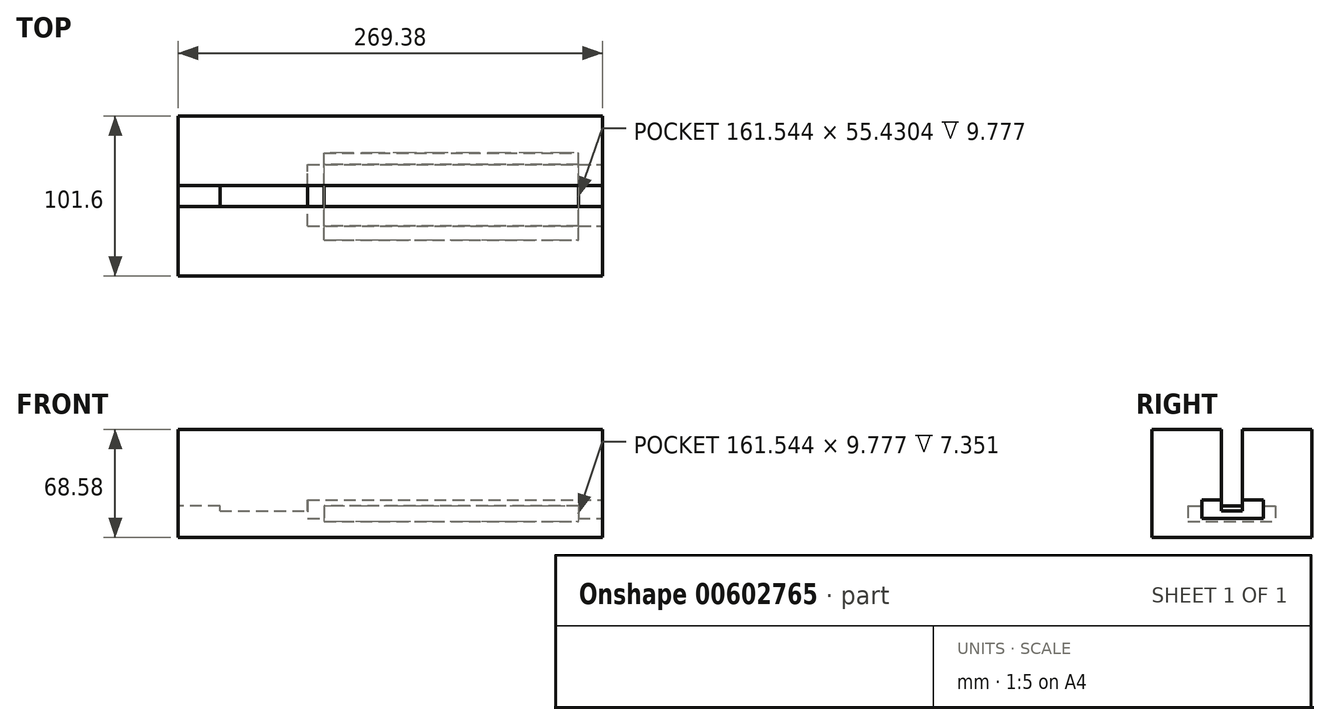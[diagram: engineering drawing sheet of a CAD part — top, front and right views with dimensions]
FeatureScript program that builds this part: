
annotation { "Feature Type Name" : "Feature", "Feature Type Description" : "" }
export const myFeature = defineFeature(function(context is Context, id is Id, definition is map)
    precondition{}
    {
        {
            var Q0;
            Q0=qCreatedBy(makeId("Top.planeOp"),FACE);
            var sketch = newSketch(context, id + "F0", { "sketchPlane" : qUnion([Q0])});
            skLineSegment(sketch, "E0.bottom", {"start": v(-134.7, 50.8) * mm, "end": v(134.7, 50.8) * mm});
            skLineSegment(sketch, "E0.top", {"start": v(-134.7, -50.8) * mm, "end": v(134.7, -50.8) * mm});
            skLineSegment(sketch, "E0.left", {"start": v(-134.7, 50.8) * mm, "end": v(-134.7, -50.8) * mm});
            skLineSegment(sketch, "E0.right", {"start": v(134.7, 50.8) * mm, "end": v(134.7, -50.8) * mm});
            skPoint(sketch, "E0.middle", {"position": v(0, 0) * mm});
            skLineSegment(sketch, "E1.bottom", {"start": v(-134.7, 34.7) * mm, "end": v(134.7, 34.7) * mm});
            skLineSegment(sketch, "E1.top", {"start": v(-134.7, -34.7) * mm, "end": v(134.7, -34.7) * mm});
            skLineSegment(sketch, "E1.left", {"start": v(-134.7, 34.7) * mm, "end": v(-134.7, -34.7) * mm});
            skLineSegment(sketch, "E1.right", {"start": v(134.7, 34.7) * mm, "end": v(134.7, -34.7) * mm});
            skSolve(sketch);
        }
        {
            var Q0;
            Q0 = qSketchRegion(id + "F0", true);
            extrude(context, id + "F1", {"entities" : qUnion([Q0]), "depth" : 68.58 * mm, "offsetDistance" : 25.4 * mm});
        }
        {
            var Q0;
            Q0=makeQuery(id+"F1.opExtrude","CAP_FACE",FACE,{"disambiguationData":[OSD([sQuery(id+"F0.wireOp",EDGE,"E0.bottom"),sQuery(id+"F0.wireOp",EDGE,"E0.top"),sQuery(id+"F0.wireOp",EDGE,"E0.left"),sQuery(id+"F0.wireOp",EDGE,"E0.right"),sQuery(id+"F0.wireOp",EDGE,"E1.left"),sQuery(id+"F0.wireOp",EDGE,"E1.right")])],"isStart":false});
            var sketch = newSketch(context, id + "F2", { "sketchPlane" : qUnion([Q0])});
            skLineSegment(sketch, "E2.bottom", {"start": v(-134.7, 6.75) * mm, "end": v(134.7, 6.75) * mm});
            skLineSegment(sketch, "E2.top", {"start": v(-134.7, -6.75) * mm, "end": v(134.7, -6.75) * mm});
            skLineSegment(sketch, "E2.left", {"start": v(-134.7, 6.75) * mm, "end": v(-134.7, -6.75) * mm});
            skLineSegment(sketch, "E2.right", {"start": v(134.7, 6.75) * mm, "end": v(134.7, -6.75) * mm});
            skPoint(sketch, "E2.middle", {"position": v(0, 0) * mm});
            skSolve(sketch);
        }
        {
            var Q0;
            Q0 = qSketchRegion(id + "F2", true);
            extrude(context, id + "F3", {"entities" : qUnion([Q0]), "operationType" : NewBodyOperationType.REMOVE, "oppositeDirection" : true, "depth" : 51.82 * mm, "offsetDistance" : 25.4 * mm});
        }
        {
            var Q0;
            Q0=makeQuery(id+"F1.opExtrude","SWEPT_FACE",FACE,{"disambiguationData":[OSD([sQuery(id+"F0.wireOp",EDGE,"E0.right"),sQuery(id+"F0.wireOp",EDGE,"E1.right")])]});
            var sketch = newSketch(context, id + "F4", { "sketchPlane" : qUnion([Q0])});
            skLineSegment(sketch, "E3.bottom", {"start": v(-27.98, 20.05) * mm, "end": v(27.45, 20.05) * mm});
            skLineSegment(sketch, "E3.top", {"start": v(-27.98, 10.28) * mm, "end": v(27.45, 10.28) * mm});
            skLineSegment(sketch, "E3.left", {"start": v(-27.98, 20.05) * mm, "end": v(-27.98, 10.28) * mm});
            skLineSegment(sketch, "E3.right", {"start": v(27.45, 20.05) * mm, "end": v(27.45, 10.28) * mm});
            skSolve(sketch);
        }
        {
            var Q0;
            Q0 = qSketchRegion(id + "F4", true);
            extrude(context, id + "F5", {"entities" : qUnion([Q0]), "operationType" : NewBodyOperationType.REMOVE, "oppositeDirection" : true, "depth" : 176.78 * mm, "offsetDistance" : 25.4 * mm});
        }
        {
            var Q0;
            Q0 = qSketchRegion(id + "F4", true);
            extrude(context, id + "F6", {"entities" : qUnion([Q0]), "operationType" : NewBodyOperationType.ADD, "oppositeDirection" : true, "depth" : 15.24 * mm, "offsetDistance" : 25.4 * mm});
        }
        {
            var Q0;
            Q0=makeQuery(id+"F1.opExtrude","SWEPT_FACE",FACE,{"disambiguationData":[OSD([sQuery(id+"F0.wireOp",EDGE,"E0.left"),sQuery(id+"F0.wireOp",EDGE,"E1.left")])]});
            var sketch = newSketch(context, id + "F7", { "sketchPlane" : qUnion([Q0])});
            skLineSegment(sketch, "E4.bottom", {"start": v(48.68, 10.28) * mm, "end": v(-6.75, 10.28) * mm});
            skLineSegment(sketch, "E4.top", {"start": v(48.68, 20.05) * mm, "end": v(-6.75, 20.05) * mm});
            skLineSegment(sketch, "E4.left", {"start": v(48.68, 10.28) * mm, "end": v(48.68, 20.05) * mm});
            skLineSegment(sketch, "E4.right", {"start": v(-6.75, 10.28) * mm, "end": v(-6.75, 20.05) * mm});
            skSolve(sketch);
        }
        {
            var Q0;
            Q0 = qSketchRegion(id + "F7", true);
            extrude(context, id + "F8", {"entities" : qUnion([Q0]), "operationType" : NewBodyOperationType.ADD, "oppositeDirection" : true, "depth" : 26.42 * mm, "offsetDistance" : 25.4 * mm});
        }
        {
            var Q0;
            Q0=makeQuery(id+"F6.boolean.opBoolean","MERGE",FACE,{"derivedFrom":[makeQuery(id+"F1.opExtrude","SWEPT_FACE",FACE,{"disambiguationData":[OSD([sQuery(id+"F0.wireOp",EDGE,"E0.right"),sQuery(id+"F0.wireOp",EDGE,"E1.right")])]}),makeQuery(id+"F6.opExtrude","CAP_FACE",FACE,{"disambiguationData":[OSD([sQuery(id+"F4.wireOp",EDGE,"E3.bottom"),sQuery(id+"F4.wireOp",EDGE,"E3.top"),sQuery(id+"F4.wireOp",EDGE,"E3.left"),sQuery(id+"F4.wireOp",EDGE,"E3.right")])],"isStart":true})]});
            var sketch = newSketch(context, id + "F9", { "sketchPlane" : qUnion([Q0])});
            skLineSegment(sketch, "E5.bottom", {"start": v(-19.02, 23.75) * mm, "end": v(20.1, 23.75) * mm});
            skLineSegment(sketch, "E5.top", {"start": v(-19.02, 12.14) * mm, "end": v(20.1, 12.14) * mm});
            skLineSegment(sketch, "E5.left", {"start": v(-19.02, 23.75) * mm, "end": v(-19.02, 12.14) * mm});
            skLineSegment(sketch, "E5.right", {"start": v(20.1, 23.75) * mm, "end": v(20.1, 12.14) * mm});
            skSolve(sketch);
        }
        {
            var Q0;
            Q0 = qSketchRegion(id + "F9", true);
            extrude(context, id + "F10", {"entities" : qUnion([Q0]), "operationType" : NewBodyOperationType.REMOVE, "oppositeDirection" : true, "depth" : 187.2 * mm, "offsetDistance" : 25.4 * mm});
        }
    });
